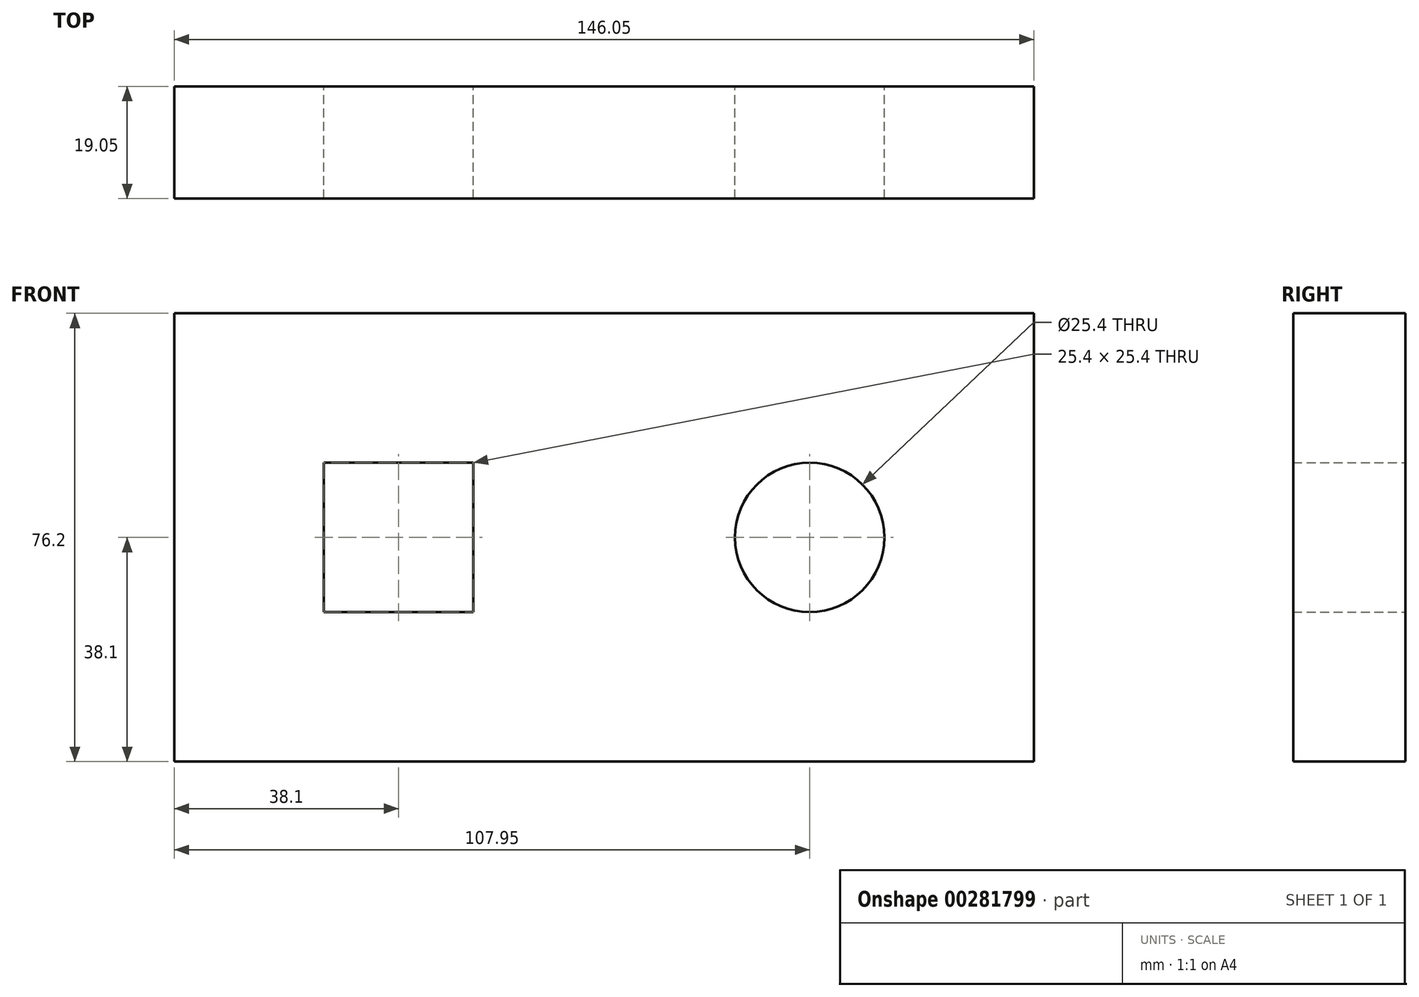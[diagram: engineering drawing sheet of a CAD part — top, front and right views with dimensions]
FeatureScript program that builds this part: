
annotation { "Feature Type Name" : "Feature", "Feature Type Description" : "" }
export const myFeature = defineFeature(function(context is Context, id is Id, definition is map)
    precondition{}
    {
        {
            var Q0;
            Q0=qCreatedBy(makeId("Front.planeOp"),FACE);
            var sketch = newSketch(context, id + "F0", { "sketchPlane" : qUnion([Q0])});
            skLineSegment(sketch, "E0.bottom", {"start": v(0, 0) * mm, "end": v(-146.05, 0) * mm});
            skLineSegment(sketch, "E0.top", {"start": v(0, 76.2) * mm, "end": v(-146.05, 76.2) * mm});
            skLineSegment(sketch, "E0.left", {"start": v(0, 0) * mm, "end": v(0, 76.2) * mm});
            skLineSegment(sketch, "E0.right", {"start": v(-146.05, 0) * mm, "end": v(-146.05, 76.2) * mm});
            skLineSegment(sketch, "E1.bottom", {"start": v(-95.25, 50.8) * mm, "end": v(-120.65, 50.8) * mm});
            skLineSegment(sketch, "E1.top", {"start": v(-95.25, 25.4) * mm, "end": v(-120.65, 25.4) * mm});
            skLineSegment(sketch, "E1.left", {"start": v(-95.25, 50.8) * mm, "end": v(-95.25, 25.4) * mm});
            skLineSegment(sketch, "E1.right", {"start": v(-120.65, 50.8) * mm, "end": v(-120.65, 25.4) * mm});
            skCircle(sketch, "E2", {"center": v(-38.1, 38.1) * mm, "radius": 12.7 * mm});
            skSolve(sketch);
        }
        {
            var Q0;
            Q0 = qSketchRegion(id + "F0", true);
            extrude(context, id + "F1", {"entities" : qUnion([Q0]), "depth" : 19.05 * mm});
        }
    });
